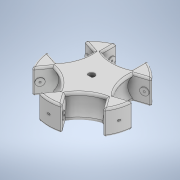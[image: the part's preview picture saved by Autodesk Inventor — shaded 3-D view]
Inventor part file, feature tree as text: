
AUTODESK INVENTOR PART (.ipt)
format: ipt  version: 2021 (Build 250183000, 183)  size: 801,280 bytes
history: native  units: in
note: dims shown in document units (in); Inventor stores cm internally (conversion verified against a paired STEP export)
features: revolve x5, fillet x3, extrude x2, mirror x1
ambient origin geometry x8: Origin, YZ Plane, XZ Plane, XY Plane, X Axis, Y Axis, Z Axis, Center Point
bodies: Solid2 (feature_tree)
feature tree (11):
  extrude  "Extrusion6"  Depth=1.9685in
  revolve  "Revolution12"  [1 undecoded]
  revolve  "Revolution13"  [1 undecoded]
  revolve  "Revolution14"  [1 undecoded]
  revolve  "Revolution15"  [1 undecoded]
  revolve  "Revolution16"  [1 undecoded]
  mirror  "Mirror1"
  extrude  "Extrusion9"  Depth=0.0354in
  fillet  "Fillet8"  Radius=0.2598in
  fillet  "Fillet9"  Radius=0.1181in
  fillet  "Fillet10"  Radius=0.096in
note: 5 required parameter values undecoded (feature->parameter linkage not recoverable at this tier; creation-order binding heuristic only, values carry confidence <= 0.55)
